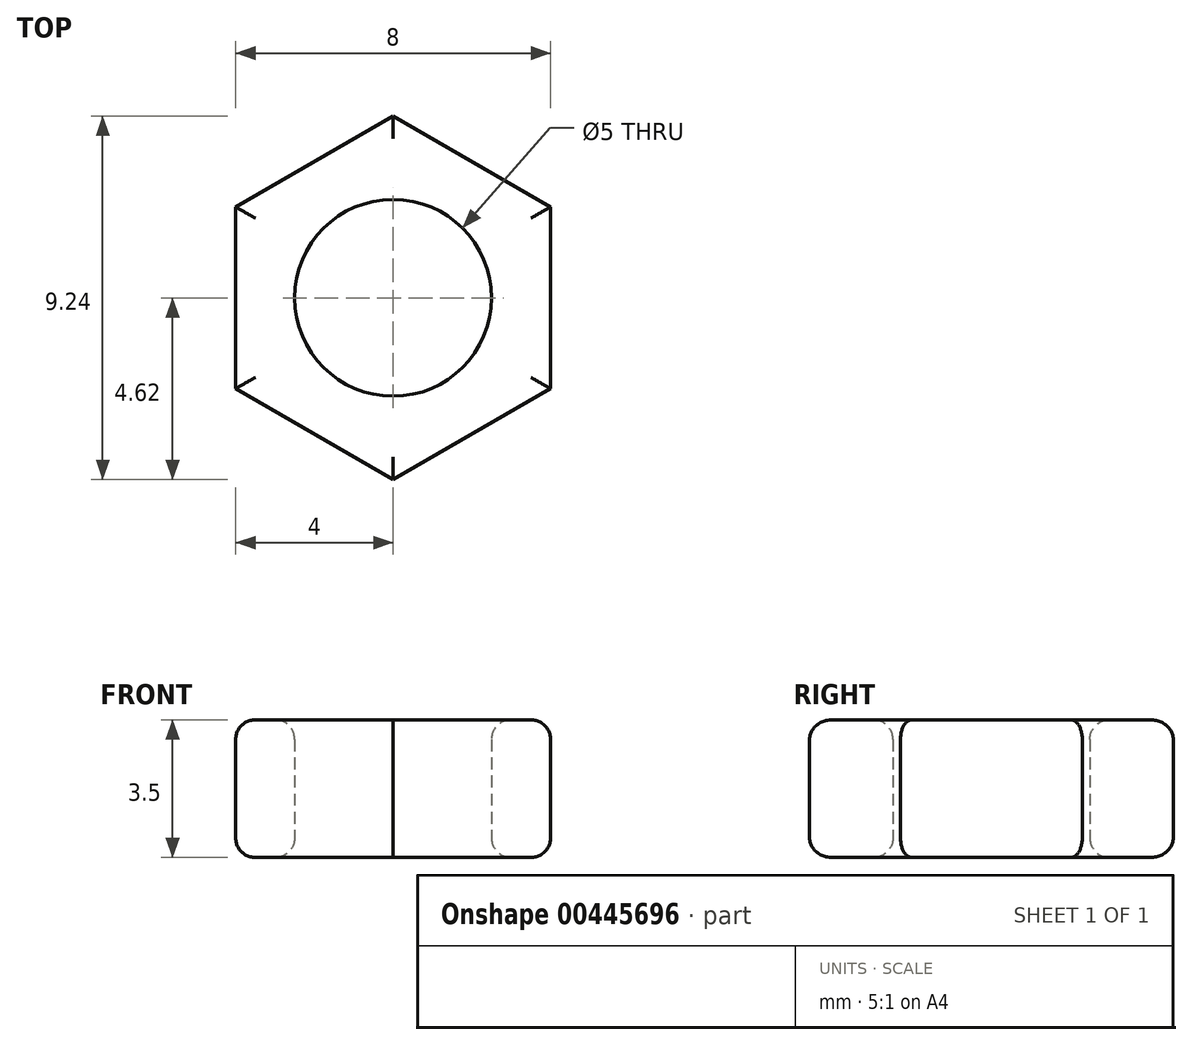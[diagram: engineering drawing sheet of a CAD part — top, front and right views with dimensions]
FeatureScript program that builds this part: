
annotation { "Feature Type Name" : "Feature", "Feature Type Description" : "" }
export const myFeature = defineFeature(function(context is Context, id is Id, definition is map)
    precondition{}
    {
        {
            var Q0;
            Q0=qCreatedBy(makeId("Top.planeOp"),FACE);
            var sketch = newSketch(context, id + "F0", { "sketchPlane" : qUnion([Q0])});
            skCircle(sketch, "E0", {"center": v(0, 0) * mm, "radius": 2.5 * mm});
            skCircle(sketch, "E1.cCircle", {"center": v(0, 0) * mm, "radius": 4 * mm, "construction": true});
            skLineSegment(sketch, "E1.0", {"start": v(4, 2.3) * mm, "end": v(4, -2.3) * mm});
            skLineSegment(sketch, "E1.1", {"start": v(4, -2.3) * mm, "end": v(0, -4.62) * mm});
            skLineSegment(sketch, "E1.2", {"start": v(0, -4.62) * mm, "end": v(-4, -2.3) * mm});
            skLineSegment(sketch, "E1.3", {"start": v(-4, -2.3) * mm, "end": v(-4, 2.3) * mm});
            skLineSegment(sketch, "E1.4", {"start": v(-4, 2.3) * mm, "end": v(0, 4.62) * mm});
            skLineSegment(sketch, "E1.5", {"start": v(0, 4.62) * mm, "end": v(4, 2.3) * mm});
            skPoint(sketch, "E1.0.midPoint", {"position": v(4, 0) * mm});
            skSolve(sketch);
        }
        {
            var Q0;
            Q0 = qSketchRegion(id + "F0", true);
            extrude(context, id + "F1", {"entities" : qUnion([Q0]), "depth" : 3.5 * mm});
        }
        {
            var Q0;
            Q0=makeQuery(id+"F1.opExtrude","CAP_FACE",FACE,{"disambiguationData":[OSD([sQuery(id+"F0.wireOp",EDGE,"E0"),sQuery(id+"F0.wireOp",EDGE,"E1.0"),sQuery(id+"F0.wireOp",EDGE,"E1.1"),sQuery(id+"F0.wireOp",EDGE,"E1.2"),sQuery(id+"F0.wireOp",EDGE,"E1.3"),sQuery(id+"F0.wireOp",EDGE,"E1.4"),sQuery(id+"F0.wireOp",EDGE,"E1.5")])],"isStart":false});
            fillet(context, id + "F2", {"entities" : qUnion([Q0]), "radius" : 0.5 * mm, "tangentPropagation" : true, "allowEdgeOverflow" : false});
        }
        {
            var Q0;
            Q0=makeQuery(id+"F1.opExtrude","CAP_FACE",FACE,{"disambiguationData":[OSD([sQuery(id+"F0.wireOp",EDGE,"E0"),sQuery(id+"F0.wireOp",EDGE,"E1.0"),sQuery(id+"F0.wireOp",EDGE,"E1.1"),sQuery(id+"F0.wireOp",EDGE,"E1.2"),sQuery(id+"F0.wireOp",EDGE,"E1.3"),sQuery(id+"F0.wireOp",EDGE,"E1.4"),sQuery(id+"F0.wireOp",EDGE,"E1.5")])],"isStart":true});
            fillet(context, id + "F3", {"entities" : qUnion([Q0]), "radius" : 0.5 * mm, "tangentPropagation" : true, "allowEdgeOverflow" : false});
        }
    });
